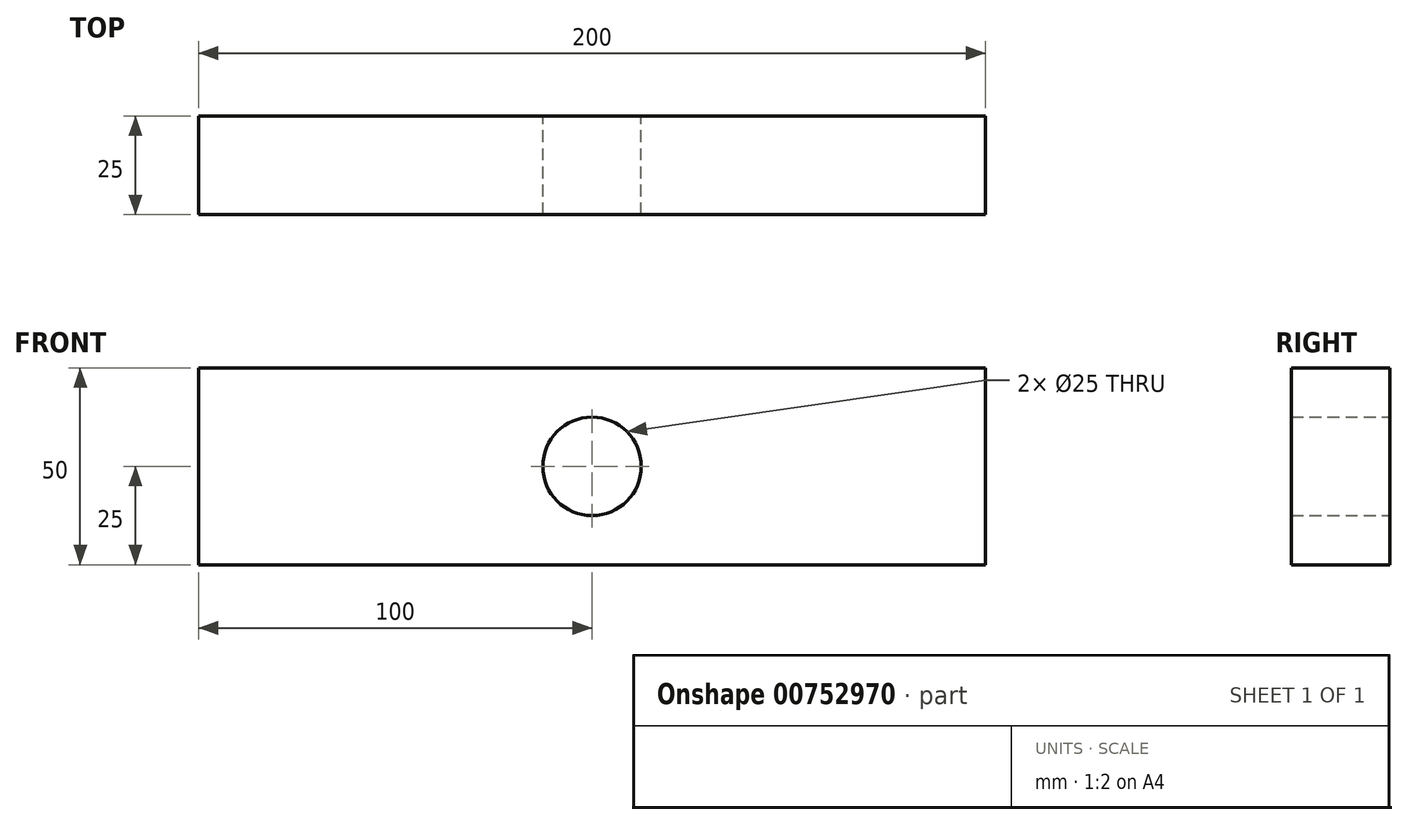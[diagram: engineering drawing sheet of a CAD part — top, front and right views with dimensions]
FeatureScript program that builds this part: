
annotation { "Feature Type Name" : "Feature", "Feature Type Description" : "" }
export const myFeature = defineFeature(function(context is Context, id is Id, definition is map)
    precondition{}
    {
        {
            var Q0;
            Q0=qCreatedBy(makeId("Front.planeOp"),FACE);
            var sketch = newSketch(context, id + "F0", { "sketchPlane" : qUnion([Q0])});
            skLineSegment(sketch, "E0.bottom", {"start": v(100, -25) * mm, "end": v(-100, -25) * mm});
            skLineSegment(sketch, "E0.top", {"start": v(100, 25) * mm, "end": v(-100, 25) * mm});
            skLineSegment(sketch, "E0.left", {"start": v(100, -25) * mm, "end": v(100, 25) * mm});
            skLineSegment(sketch, "E0.right", {"start": v(-100, -25) * mm, "end": v(-100, 25) * mm});
            skPoint(sketch, "E0.middle", {"position": v(0, 0) * mm});
            skCircle(sketch, "E1", {"center": v(0, 0) * mm, "radius": 12.5 * mm});
            skSolve(sketch);
        }
        {
            var Q0;
            Q0 = qSketchRegion(id + "F0", true);
            extrude(context, id + "F1", {"entities" : qUnion([Q0]), "depth" : 25 * mm, "offsetDistance" : 25 * mm});
        }
    });
